# Revit family: Shower-Valve_Trim-KOHLER-Forte-K-TS10277
name_source: partatom
category: Specialty Equipment
revit_build: Autodesk Revit 2015 (Build: 20140606_1530(x64)
units: mm (PartAtom-declared; Revit-internal decimal feet)

## types (6) — shared parameters
ADA Compliant = Yes
Assembly Code = C1030200
Date Modified = 06/09/2018
Default Elevation = 42"
Height = 6 3/8"
Length = 5"
Manufacturer = KOHLER Co.
MasterFormat 1995 = 10820
MasterFormat 2004 = 10.28.13
Material = Premium Metal Construction
Product Documentation Link = http://www.us.kohler.com
Product Name = Forte
Product Page URL = http://www.us.kohler.com
URL = https://www.us.kohler.com
Width = 6 3/8"

## per-type parameters (varying)
| type | Description | Finish | Model | Sculpted Lever Handle | Traditional Lever Handle | Type |
| Sculpted Lever Handle,CP-Polished Chrome | Sculpted rite-temp valve trim | Kohler-Metal-CP-Polished_Chrome | K-TS10277-4-CP | Yes | No | 1 |
| Sculpted Lever Handle,G-Brushed Chrome | Sculpted rite-temp valve trim | Kohler-Metal-G-Brushed_Chrome | K-TS10277-4-G | Yes | No | 2 |
| Sculpted Lever Handle,BN-Vibrant Brushed Nickel | Sculpted rite-temp valve trim | Kohler-Metal-BN-Vibrant_Brushed_Nickel | K-TS10277-4-BN | Yes | No | 3 |
| Traditional Lever Handle,CP-Polished Chrome | Traditional rite-temp valve trim | Kohler-Metal-CP-Polished_Chrome | K-TS10277-4A-CP | No | Yes | 4 |
| Traditional Lever Handle,G-Brushed Chrome | Traditional rite-temp valve trim | Kohler-Metal-G-Brushed_Chrome | K-10277-4A-G | No | Yes | 5 |
| Traditional Lever Handle,BN-Vibrant Brushed Nickel | Traditional rite-temp valve trim | Kohler-Metal-BN-Vibrant_Brushed_Nickel | K-10277-4A-BN | No | Yes | 6 |

## geometry (parser evidence)
native form markers: Sweep x5
no freeform markers — native parametric forms only
